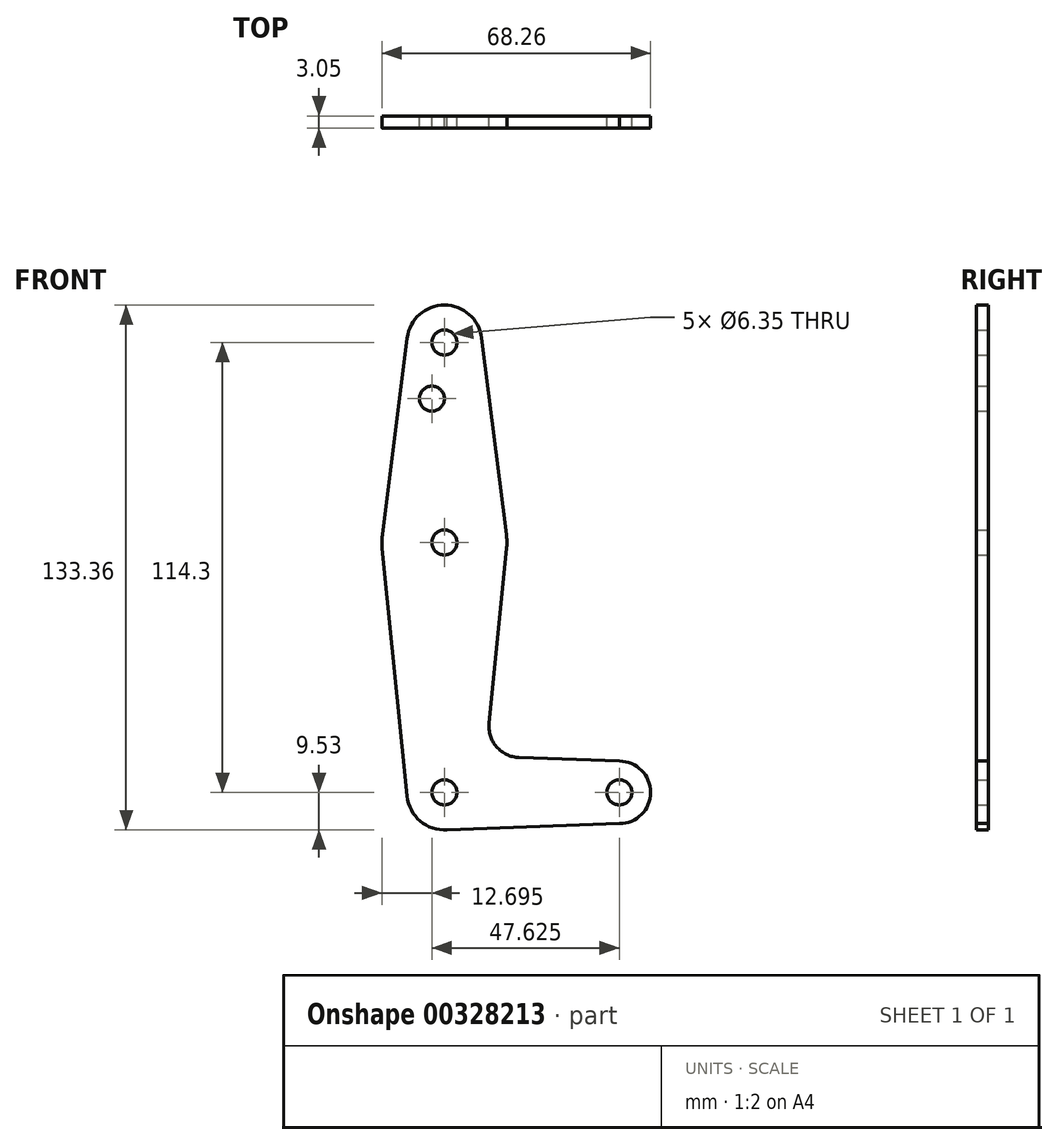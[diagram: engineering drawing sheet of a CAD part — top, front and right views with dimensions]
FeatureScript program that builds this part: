
annotation { "Feature Type Name" : "Feature", "Feature Type Description" : "" }
export const myFeature = defineFeature(function(context is Context, id is Id, definition is map)
    precondition{}
    {
        {
            var Q0;
            Q0=qCreatedBy(makeId("Front.planeOp"),FACE);
            var sketch = newSketch(context, id + "F0", { "sketchPlane" : qUnion([Q0])});
            skLineSegment(sketch, "E0", {"start": v(0, 0) * mm, "end": v(0, 114.3) * mm, "construction": true});
            skLineSegment(sketch, "E1", {"start": v(0, 0) * mm, "end": v(44.45, 0) * mm, "construction": true});
            skCircle(sketch, "E2", {"center": v(0, 114.3) * mm, "radius": 9.53 * mm});
            skCircle(sketch, "E3", {"center": v(0, 0) * mm, "radius": 9.53 * mm});
            skCircle(sketch, "E4", {"center": v(44.45, 0) * mm, "radius": 7.94 * mm});
            skCircle(sketch, "E5", {"center": v(0, 63.5) * mm, "radius": 15.88 * mm});
            skLineSegment(sketch, "E6", {"start": v(9.45, 115.5) * mm, "end": v(15.75, 65.48) * mm});
            skLineSegment(sketch, "E7", {"start": v(-15.8, 61.91) * mm, "end": v(-9.48, -0.95) * mm});
            skLineSegment(sketch, "E8", {"start": v(0, -9.53) * mm, "end": v(44.45, -7.94) * mm});
            skLineSegment(sketch, "E9", {"start": v(-9.45, 115.5) * mm, "end": v(-15.75, 65.48) * mm});
            skCircle(sketch, "E10", {"center": v(0, 114.3) * mm, "radius": 3.18 * mm});
            skCircle(sketch, "E11", {"center": v(0, 63.5) * mm, "radius": 3.18 * mm});
            skCircle(sketch, "E12", {"center": v(0, 0) * mm, "radius": 3.18 * mm});
            skCircle(sketch, "E13", {"center": v(44.45, 0) * mm, "radius": 3.18 * mm});
            skCircle(sketch, "E14", {"center": v(-3.18, 100.03) * mm, "radius": 3.18 * mm});
            skLineSegment(sketch, "E15", {"start": v(44.45, 7.94) * mm, "end": v(18.97, 8.85) * mm});
            skLineSegment(sketch, "E16", {"start": v(15.8, 61.91) * mm, "end": v(11.34, 17.6) * mm});
            skPoint(sketch, "E17.newPointB", {"position": v(0, 9.53) * mm});
            skArc(sketch, "E17.filletArc", {"start": v(11.34, 17.6) * mm, "mid": v(13.26, 11.57) * mm, "end": v(18.97, 8.85) * mm});
            skSolve(sketch);
        }
        {
            var Q0;
            Q0 = qSketchRegion(id + "F0", true);
            extrude(context, id + "F1", {"entities" : qUnion([Q0]), "depth" : 3.05 * mm});
        }
    });
